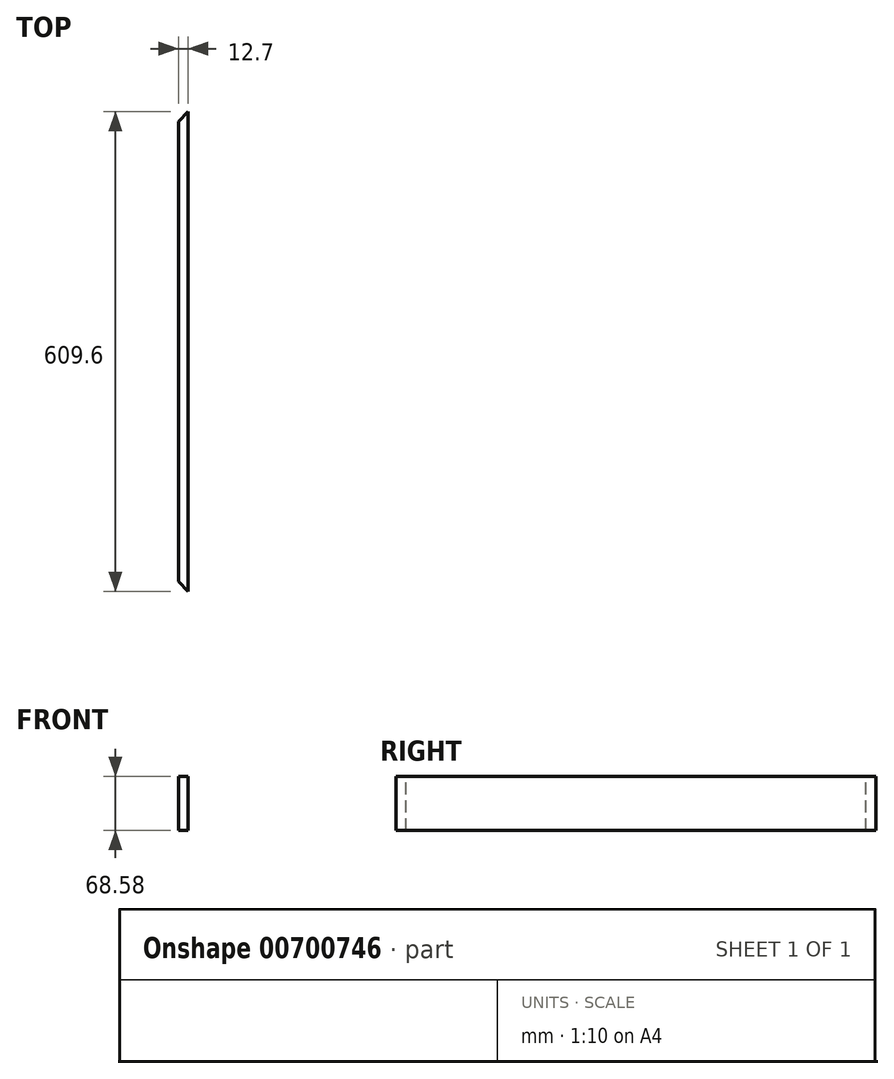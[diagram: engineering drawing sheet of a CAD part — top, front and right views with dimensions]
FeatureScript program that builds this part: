
annotation { "Feature Type Name" : "Feature", "Feature Type Description" : "" }
export const myFeature = defineFeature(function(context is Context, id is Id, definition is map)
    precondition{}
    {
        {
            var Q0;
            Q0=qCreatedBy(makeId("Right.planeOp"),FACE);
            var sketch = newSketch(context, id + "F0", { "sketchPlane" : qUnion([Q0])});
            skLineSegment(sketch, "E0.bottom", {"start": v(0, 0) * mm, "end": v(609.6, 0) * mm});
            skLineSegment(sketch, "E0.top", {"start": v(0, 68.58) * mm, "end": v(609.6, 68.58) * mm});
            skLineSegment(sketch, "E0.left", {"start": v(0, 0) * mm, "end": v(0, 68.58) * mm});
            skLineSegment(sketch, "E0.right", {"start": v(609.6, 0) * mm, "end": v(609.6, 68.58) * mm});
            skSolve(sketch);
        }
        {
            var Q0;
            Q0 = qSketchRegion(id + "F0", true);
            extrude(context, id + "F1", {"entities" : qUnion([Q0]), "depth" : 12.7 * mm, "offsetDistance" : 25.4 * mm});
        }
        {
            var Q0;
            Q0=makeQuery(id+"F1.opExtrude","SWEPT_FACE",FACE,{"disambiguationData":[OSD([sQuery(id+"F0.wireOp",EDGE,"E0.top")])]});
            var sketch = newSketch(context, id + "F2", { "sketchPlane" : qUnion([Q0])});
            skLineSegment(sketch, "E1", {"start": v(12.7, 0) * mm, "end": v(0, 12.7) * mm});
            skLineSegment(sketch, "E2", {"start": v(0, 12.7) * mm, "end": v(0, 0) * mm});
            skLineSegment(sketch, "E3", {"start": v(0, 0) * mm, "end": v(12.7, 0) * mm});
            skLineSegment(sketch, "E4", {"start": v(12.7, 609.6) * mm, "end": v(0, 596.9) * mm});
            skLineSegment(sketch, "E5", {"start": v(0, 596.9) * mm, "end": v(0, 609.6) * mm});
            skLineSegment(sketch, "E6", {"start": v(0, 609.6) * mm, "end": v(12.7, 609.6) * mm});
            skSolve(sketch);
        }
        {
            var Q0;
            Q0 = qSketchRegion(id + "F2", true);
            extrude(context, id + "F3", {"entities" : qUnion([Q0]), "operationType" : NewBodyOperationType.REMOVE, "endBound" : BoundingType.THROUGH_ALL, "oppositeDirection" : true, "depth" : 25.4 * mm, "offsetDistance" : 25.4 * mm});
        }
    });
